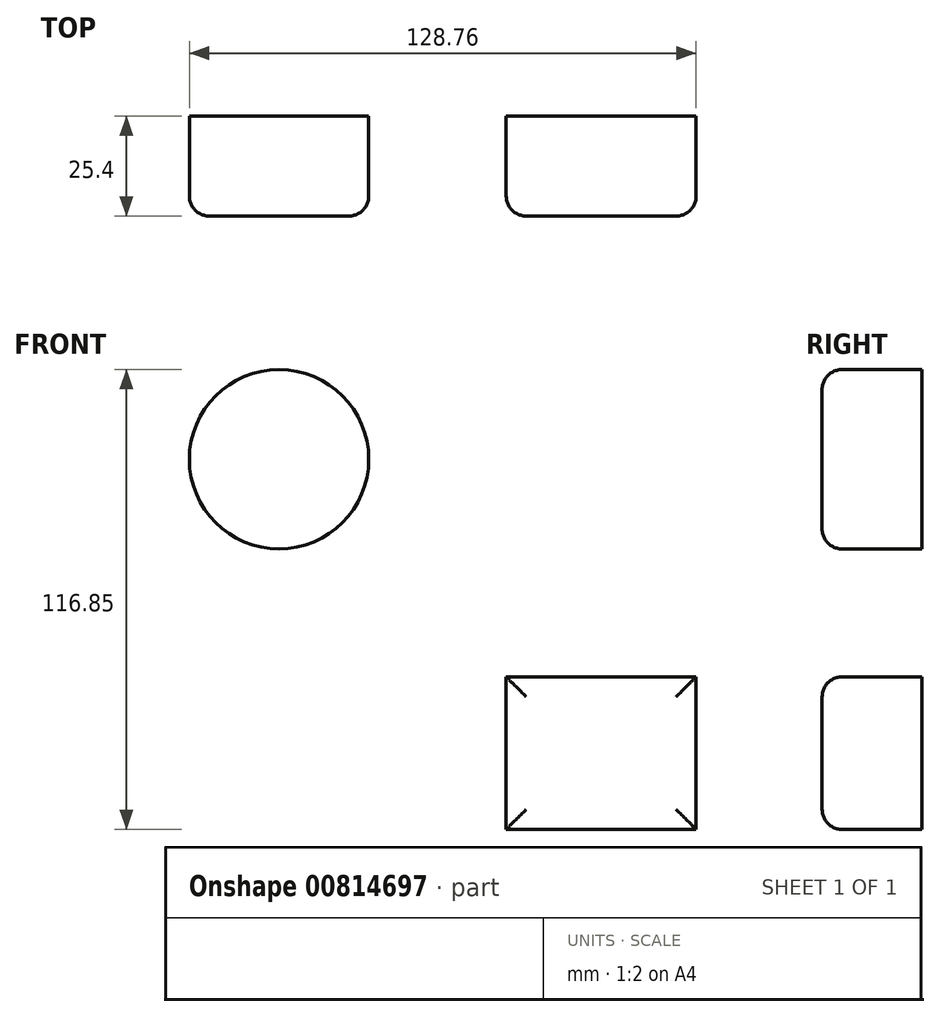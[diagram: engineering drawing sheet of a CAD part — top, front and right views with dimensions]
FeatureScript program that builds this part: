
annotation { "Feature Type Name" : "Feature", "Feature Type Description" : "" }
export const myFeature = defineFeature(function(context is Context, id is Id, definition is map)
    precondition{}
    {
        {
            var Q0;
            Q0=qCreatedBy(makeId("Front.planeOp"),FACE);
            var sketch = newSketch(context, id + "F0", { "sketchPlane" : qUnion([Q0])});
            skCircle(sketch, "E0", {"center": v(-37.4, 30.7) * mm, "radius": 22.79 * mm});
            skLineSegment(sketch, "E1.bottom", {"start": v(20.3, -24.58) * mm, "end": v(68.56, -24.58) * mm});
            skLineSegment(sketch, "E1.top", {"start": v(20.3, -63.37) * mm, "end": v(68.56, -63.37) * mm});
            skLineSegment(sketch, "E1.left", {"start": v(20.3, -24.58) * mm, "end": v(20.3, -63.37) * mm});
            skLineSegment(sketch, "E1.right", {"start": v(68.56, -24.58) * mm, "end": v(68.56, -63.37) * mm});
            skSolve(sketch);
        }
        {
            var Q0;
            Q0=makeQuery(id+"F0.imprint","IMPRINT",FACE,{"disambiguationData":[TD([[makeQuery(id+"F0.imprint","IMPRINT",EDGE,{"derivedFrom":sQuery(id+"F0.wireOp",EDGE,"E0")}),1.0]])]});
            var Q1;
            Q1=makeQuery(id+"F0.imprint","IMPRINT",FACE,{"disambiguationData":[TD([[makeQuery(id+"F0.imprint","IMPRINT",EDGE,{"derivedFrom":sQuery(id+"F0.wireOp",EDGE,"E1.bottom")}),-1.0]])]});
            extrude(context, id + "F1", {"entities" : qUnion([Q0, Q1]), "depth" : 25.4 * mm, "offsetDistance" : 25.4 * mm});
        }
        {
            var Q0;
            Q0=makeQuery(id+"F1.opExtrude","CAP_FACE",FACE,{"disambiguationData":[OSD([sQuery(id+"F0.wireOp",EDGE,"E0")])],"isStart":false});
            var Q1;
            Q1=makeQuery(id+"F1.opExtrude","CAP_FACE",FACE,{"disambiguationData":[OSD([sQuery(id+"F0.wireOp",EDGE,"E1.bottom"),sQuery(id+"F0.wireOp",EDGE,"E1.top"),sQuery(id+"F0.wireOp",EDGE,"E1.left"),sQuery(id+"F0.wireOp",EDGE,"E1.right")])],"isStart":false});
            fillet(context, id + "F2", {"entities" : qUnion([Q0, Q1]), "radius" : 5.08 * mm, "tangentPropagation" : true, "allowEdgeOverflow" : false});
        }
    });
